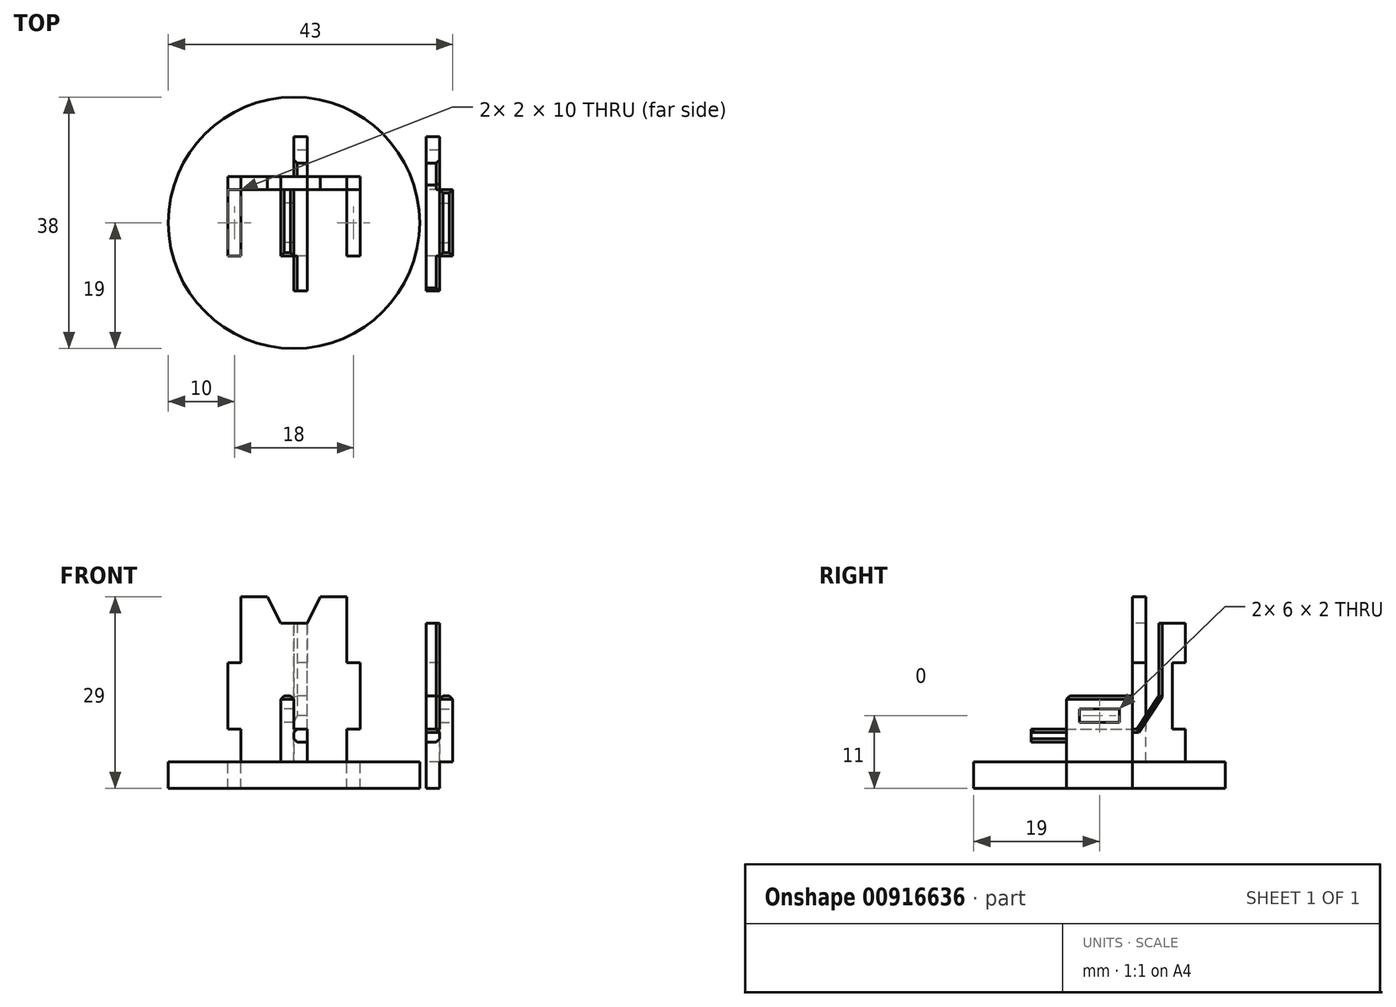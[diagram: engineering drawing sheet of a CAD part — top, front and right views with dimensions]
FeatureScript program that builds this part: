
annotation { "Feature Type Name" : "Feature", "Feature Type Description" : "" }
export const myFeature = defineFeature(function(context is Context, id is Id, definition is map)
    precondition{}
    {
        {
            var Q0;
            Q0=qCreatedBy(makeId("Top.planeOp"),FACE);
            var sketch = newSketch(context, id + "F0", { "sketchPlane" : qUnion([Q0])});
            skCircle(sketch, "E0", {"center": v(0, 0) * mm, "radius": 19 * mm});
            skSolve(sketch);
        }
        {
            var Q0;
            Q0=makeQuery(id+"F0.imprint","IMPRINT",FACE,{"disambiguationData":[TD([[makeQuery(id+"F0.imprint","IMPRINT",EDGE,{"derivedFrom":sQuery(id+"F0.wireOp",EDGE,"E0")}),1.0]])]});
            extrude(context, id + "F1", {"entities" : qUnion([Q0]), "depth" : 4 * mm, "offsetDistance" : 25 * mm});
        }
        {
            var Q0;
            Q0=makeQuery(id+"F1.opExtrude","CAP_FACE",FACE,{"disambiguationData":[OSD([sQuery(id+"F0.wireOp",EDGE,"E0")])],"isStart":false});
            var sketch = newSketch(context, id + "F2", { "sketchPlane" : qUnion([Q0])});
            skLineSegment(sketch, "E1.bottom", {"start": v(-10, 5) * mm, "end": v(-8, 5) * mm});
            skLineSegment(sketch, "E1.top", {"start": v(-10, -5) * mm, "end": v(-8, -5) * mm});
            skLineSegment(sketch, "E1.left", {"start": v(-10, 5) * mm, "end": v(-10, -5) * mm});
            skLineSegment(sketch, "E1.right", {"start": v(-8, 5) * mm, "end": v(-8, -5) * mm});
            skLineSegment(sketch, "E2", {"start": v(0, -13.87) * mm, "end": v(0, 16.66) * mm, "construction": true});
            skLineSegment(sketch, "E3.MirrorCS", {"start": v(10, 5) * mm, "end": v(8, 5) * mm});
            skLineSegment(sketch, "E4.MirrorCS", {"start": v(10, 5) * mm, "end": v(10, -5) * mm});
            skLineSegment(sketch, "E5.MirrorCS", {"start": v(8, 5) * mm, "end": v(8, -5) * mm});
            skLineSegment(sketch, "E6.MirrorCS", {"start": v(10, -5) * mm, "end": v(8, -5) * mm});
            skSolve(sketch);
        }
        {
            var Q0;
            Q0=makeQuery(id+"F2.imprint","IMPRINT",FACE,{"disambiguationData":[TD([[makeQuery(id+"F2.imprint","IMPRINT",EDGE,{"derivedFrom":sQuery(id+"F2.wireOp",EDGE,"E1.bottom")}),-1.0]])]});
            var Q1;
            Q1=makeQuery(id+"F2.imprint","IMPRINT",FACE,{"disambiguationData":[TD([[makeQuery(id+"F2.imprint","IMPRINT",EDGE,{"derivedFrom":sQuery(id+"F2.wireOp",EDGE,"E3.MirrorCS")}),1.0]])]});
            extrude(context, id + "F3", {"entities" : qUnion([Q0, Q1]), "operationType" : NewBodyOperationType.REMOVE, "endBound" : BoundingType.THROUGH_ALL, "oppositeDirection" : true, "depth" : 4 * mm, "offsetDistance" : 25 * mm});
        }
        {
            var Q0;
            Q0=qCreatedBy(makeId("Right.planeOp"),FACE);
            var sketch = newSketch(context, id + "F4", { "sketchPlane" : qUnion([Q0])});
            skLineSegment(sketch, "E7", {"start": v(-5, 0) * mm, "end": v(-5, 4) * mm});
            skLineSegment(sketch, "E8", {"start": v(-5, 4) * mm, "end": v(-5, 7) * mm});
            skLineSegment(sketch, "E9", {"start": v(-5, 7) * mm, "end": v(-10.32, 7) * mm});
            skLineSegment(sketch, "E10", {"start": v(-10.32, 7) * mm, "end": v(-10.32, 9) * mm});
            skLineSegment(sketch, "E11", {"start": v(-10.32, 9) * mm, "end": v(5.68, 9) * mm});
            skLineSegment(sketch, "E12", {"start": v(5.68, 9) * mm, "end": v(9, 14) * mm});
            skLineSegment(sketch, "E13", {"start": v(9, 14) * mm, "end": v(9, 29) * mm});
            skLineSegment(sketch, "E14", {"start": v(9, 29) * mm, "end": v(13, 29) * mm});
            skLineSegment(sketch, "E15", {"start": v(13, 29) * mm, "end": v(13, 4) * mm});
            skLineSegment(sketch, "E16", {"start": v(13, 4) * mm, "end": v(5, 4) * mm});
            skLineSegment(sketch, "E17", {"start": v(5, 4) * mm, "end": v(5, 0) * mm});
            skLineSegment(sketch, "E18", {"start": v(5, 0) * mm, "end": v(-5, 0) * mm});
            skSolve(sketch);
        }
        {
            var Q0;
            Q0=makeQuery(id+"F4.imprint","IMPRINT",FACE,{"disambiguationData":[TD([[makeQuery(id+"F4.imprint","IMPRINT",EDGE,{"derivedFrom":sQuery(id+"F4.wireOp",EDGE,"E7")}),-1.0]])]});
            extrude(context, id + "F5", {"entities" : qUnion([Q0]), "depth" : 2 * mm, "offsetDistance" : 25 * mm});
        }
        {
            var Q0;
            Q0=makeQuery(id+"F5.opExtrude","CAP_FACE",FACE,{"disambiguationData":[OSD([sQuery(id+"F4.wireOp",EDGE,"E7"),sQuery(id+"F4.wireOp",EDGE,"E8"),sQuery(id+"F4.wireOp",EDGE,"E9"),sQuery(id+"F4.wireOp",EDGE,"E10"),sQuery(id+"F4.wireOp",EDGE,"E11"),sQuery(id+"F4.wireOp",EDGE,"E12"),sQuery(id+"F4.wireOp",EDGE,"E13"),sQuery(id+"F4.wireOp",EDGE,"E14"),sQuery(id+"F4.wireOp",EDGE,"E15"),sQuery(id+"F4.wireOp",EDGE,"E16"),sQuery(id+"F4.wireOp",EDGE,"E17"),sQuery(id+"F4.wireOp",EDGE,"E18")])],"isStart":true});
            var sketch = newSketch(context, id + "F6", { "sketchPlane" : qUnion([Q0])});
            skLineSegment(sketch, "E19.bottom", {"start": v(-13, 19) * mm, "end": v(-11, 19) * mm});
            skLineSegment(sketch, "E19.top", {"start": v(-13, 9) * mm, "end": v(-11, 9) * mm});
            skLineSegment(sketch, "E19.left", {"start": v(-13, 19) * mm, "end": v(-13, 9) * mm});
            skLineSegment(sketch, "E19.right", {"start": v(-11, 19) * mm, "end": v(-11, 9) * mm});
            skSolve(sketch);
        }
        {
            var Q0;
            Q0=makeQuery(id+"F1.opExtrude","CAP_FACE",FACE,{"disambiguationData":[OSD([sQuery(id+"F0.wireOp",EDGE,"E0")])],"isStart":false});
            var sketch = newSketch(context, id + "F7", { "sketchPlane" : qUnion([Q0])});
            skLineSegment(sketch, "E20.bottom", {"start": v(-10, 5) * mm, "end": v(10, 5) * mm});
            skLineSegment(sketch, "E20.top", {"start": v(-10, 7) * mm, "end": v(10, 7) * mm});
            skLineSegment(sketch, "E20.left", {"start": v(-10, 5) * mm, "end": v(-10, 7) * mm});
            skLineSegment(sketch, "E20.right", {"start": v(10, 5) * mm, "end": v(10, 7) * mm});
            skSolve(sketch);
        }
        {
            var Q0;
            Q0=makeQuery(id+"F7.imprint","IMPRINT",FACE,{"disambiguationData":[TD([[makeQuery(id+"F7.imprint","IMPRINT",EDGE,{"derivedFrom":sQuery(id+"F7.wireOp",EDGE,"E20.top")}),-1.0]])]});
            extrude(context, id + "F8", {"entities" : qUnion([Q0]), "depth" : 25 * mm, "offsetDistance" : 25 * mm});
        }
        {
            var Q0;
            Q0=makeQuery(id+"F8.opExtrude","SWEPT_FACE",FACE,{"disambiguationData":[OSD([sQuery(id+"F7.wireOp",EDGE,"E20.top")])]});
            var sketch = newSketch(context, id + "F9", { "sketchPlane" : qUnion([Q0])});
            skLineSegment(sketch, "E21.bottom", {"start": v(-10, 29) * mm, "end": v(-8, 29) * mm});
            skLineSegment(sketch, "E21.top", {"start": v(-10, 19) * mm, "end": v(-8, 19) * mm});
            skLineSegment(sketch, "E21.left", {"start": v(-10, 29) * mm, "end": v(-10, 19) * mm});
            skLineSegment(sketch, "E21.right", {"start": v(-8, 29) * mm, "end": v(-8, 19) * mm});
            skLineSegment(sketch, "E22.bottom", {"start": v(10, 29) * mm, "end": v(8, 29) * mm});
            skLineSegment(sketch, "E22.top", {"start": v(10, 19) * mm, "end": v(8, 19) * mm});
            skLineSegment(sketch, "E22.left", {"start": v(10, 29) * mm, "end": v(10, 19) * mm});
            skLineSegment(sketch, "E22.right", {"start": v(8, 29) * mm, "end": v(8, 19) * mm});
            skLineSegment(sketch, "E23.bottom", {"start": v(-10, 4) * mm, "end": v(-8, 4) * mm});
            skLineSegment(sketch, "E23.top", {"start": v(-10, 9) * mm, "end": v(-8, 9) * mm});
            skLineSegment(sketch, "E23.left", {"start": v(-10, 4) * mm, "end": v(-10, 9) * mm});
            skLineSegment(sketch, "E23.right", {"start": v(-8, 4) * mm, "end": v(-8, 9) * mm});
            skLineSegment(sketch, "E24.bottom", {"start": v(10, 4) * mm, "end": v(8, 4) * mm});
            skLineSegment(sketch, "E24.top", {"start": v(10, 9) * mm, "end": v(8, 9) * mm});
            skLineSegment(sketch, "E24.left", {"start": v(10, 4) * mm, "end": v(10, 9) * mm});
            skLineSegment(sketch, "E24.right", {"start": v(8, 4) * mm, "end": v(8, 9) * mm});
            skSolve(sketch);
        }
        {
            var Q0;
            Q0=makeQuery(id+"F9.imprint","IMPRINT",FACE,{"disambiguationData":[TD([[makeQuery(id+"F9.imprint","IMPRINT",EDGE,{"derivedFrom":sQuery(id+"F9.wireOp",EDGE,"E21.bottom")}),1.0]])]});
            var Q1;
            Q1=makeQuery(id+"F9.imprint","IMPRINT",FACE,{"disambiguationData":[TD([[makeQuery(id+"F9.imprint","IMPRINT",EDGE,{"derivedFrom":sQuery(id+"F9.wireOp",EDGE,"E22.bottom")}),1.0]])]});
            var Q2;
            Q2=makeQuery(id+"F9.imprint","IMPRINT",FACE,{"disambiguationData":[TD([[makeQuery(id+"F9.imprint","IMPRINT",EDGE,{"derivedFrom":sQuery(id+"F9.wireOp",EDGE,"E24.bottom")}),-1.0]])]});
            var Q3;
            Q3=makeQuery(id+"F9.imprint","IMPRINT",FACE,{"disambiguationData":[TD([[makeQuery(id+"F9.imprint","IMPRINT",EDGE,{"derivedFrom":sQuery(id+"F9.wireOp",EDGE,"E23.bottom")}),-1.0]])]});
            extrude(context, id + "F10", {"entities" : qUnion([Q0, Q1, Q2, Q3]), "operationType" : NewBodyOperationType.REMOVE, "endBound" : BoundingType.THROUGH_ALL, "oppositeDirection" : true, "depth" : 25 * mm, "offsetDistance" : 25 * mm});
        }
        {
            var Q0;
            Q0=makeQuery(id+"F6.imprint","IMPRINT",FACE,{"disambiguationData":[TD([[makeQuery(id+"F6.imprint","IMPRINT",EDGE,{"derivedFrom":sQuery(id+"F6.wireOp",EDGE,"E19.bottom")}),-1.0]])]});
            extrude(context, id + "F11", {"entities" : qUnion([Q0]), "operationType" : NewBodyOperationType.REMOVE, "endBound" : BoundingType.THROUGH_ALL, "oppositeDirection" : true, "depth" : 25 * mm, "offsetDistance" : 25 * mm});
        }
        {
            var Q0;
            Q0=makeQuery(id+"F8.opExtrude","SWEPT_FACE",FACE,{"disambiguationData":[OSD([sQuery(id+"F7.wireOp",EDGE,"E20.bottom")])]});
            var sketch = newSketch(context, id + "F12", { "sketchPlane" : qUnion([Q0])});
            skLineSegment(sketch, "E25", {"start": v(-4, 29) * mm, "end": v(-2, 25) * mm});
            skLineSegment(sketch, "E26", {"start": v(-2, 25) * mm, "end": v(2, 25) * mm});
            skLineSegment(sketch, "E27", {"start": v(2, 25) * mm, "end": v(4, 29) * mm});
            skLineSegment(sketch, "E28", {"start": v(4, 29) * mm, "end": v(-4, 29) * mm});
            skSolve(sketch);
        }
        {
            var Q0;
            Q0=makeQuery(id+"F12.imprint","IMPRINT",FACE,{"disambiguationData":[TD([[makeQuery(id+"F12.imprint","IMPRINT",EDGE,{"derivedFrom":sQuery(id+"F12.wireOp",EDGE,"E25")}),1.0]])]});
            extrude(context, id + "F13", {"entities" : qUnion([Q0]), "operationType" : NewBodyOperationType.REMOVE, "endBound" : BoundingType.THROUGH_ALL, "oppositeDirection" : true, "depth" : 25 * mm, "offsetDistance" : 25 * mm});
        }
        {
            var Q0;
            Q0=makeQuery(id+"F5.opExtrude","SWEPT_BODY",BODY,{"disambiguationData":[OSD([sQuery(id+"F4.wireOp",EDGE,"E7"),sQuery(id+"F4.wireOp",EDGE,"E8"),sQuery(id+"F4.wireOp",EDGE,"E9"),sQuery(id+"F4.wireOp",EDGE,"E10"),sQuery(id+"F4.wireOp",EDGE,"E11"),sQuery(id+"F4.wireOp",EDGE,"E12"),sQuery(id+"F4.wireOp",EDGE,"E13"),sQuery(id+"F4.wireOp",EDGE,"E14"),sQuery(id+"F4.wireOp",EDGE,"E15"),sQuery(id+"F4.wireOp",EDGE,"E16"),sQuery(id+"F4.wireOp",EDGE,"E17"),sQuery(id+"F4.wireOp",EDGE,"E18")])]});
            transform(context, id + "F14", {"entities" : qUnion([Q0]), "transformType" : TransformType.TRANSLATION_3D, "dx" : 20 * mm, "dy" : 0 * mm, "dz" : 0 * mm, "makeCopy" : true});
        }
        {
            var Q0;
            Q0=makeQuery(id+"F5.opExtrude","CAP_FACE",FACE,{"disambiguationData":[OSD([sQuery(id+"F4.wireOp",EDGE,"E7"),sQuery(id+"F4.wireOp",EDGE,"E8"),sQuery(id+"F4.wireOp",EDGE,"E9"),sQuery(id+"F4.wireOp",EDGE,"E10"),sQuery(id+"F4.wireOp",EDGE,"E11"),sQuery(id+"F4.wireOp",EDGE,"E12"),sQuery(id+"F4.wireOp",EDGE,"E13"),sQuery(id+"F4.wireOp",EDGE,"E14"),sQuery(id+"F4.wireOp",EDGE,"E15"),sQuery(id+"F4.wireOp",EDGE,"E16"),sQuery(id+"F4.wireOp",EDGE,"E17"),sQuery(id+"F4.wireOp",EDGE,"E18")])],"isStart":true});
            var sketch = newSketch(context, id + "F15", { "sketchPlane" : qUnion([Q0])});
            skLineSegment(sketch, "E29.bottom", {"start": v(-5, 4) * mm, "end": v(5, 4) * mm});
            skLineSegment(sketch, "E29.top", {"start": v(-5, 14) * mm, "end": v(5, 14) * mm});
            skLineSegment(sketch, "E29.left", {"start": v(-5, 4) * mm, "end": v(-5, 14) * mm});
            skLineSegment(sketch, "E29.right", {"start": v(5, 4) * mm, "end": v(5, 14) * mm});
            skSolve(sketch);
        }
        {
            var Q0;
            {var subQ0=sQuery(id+"F15.wireOp",EDGE,"E29.top");Q0=makeQuery(id+"F15.imprint","IMPRINT",FACE,{"disambiguationData":[TD([[makeQuery(id+"F15.imprint","IMPRINT",EDGE,{"derivedFrom":subQ0}),-1.0]])]});}
            var Q1;
            {var subQ2=sQuery(id+"F15.wireOp",EDGE,"E29.bottom");Q1=makeQuery(id+"F15.imprint","IMPRINT",FACE,{"disambiguationData":[TD([[makeQuery(id+"F15.imprint","IMPRINT",EDGE,{"derivedFrom":subQ2}),1.0]])]});}
            extrude(context, id + "F16", {"entities" : qUnion([Q0, Q1]), "operationType" : NewBodyOperationType.ADD, "depth" : 2 * mm, "offsetDistance" : 25 * mm});
        }
        {
            var Q0;
            Q0=makeQuery(id+"F16.opExtrude","CAP_FACE",FACE,{"disambiguationData":[OSD([sQuery(id+"F15.wireOp",EDGE,"E29.bottom"),sQuery(id+"F15.wireOp",EDGE,"E29.top"),sQuery(id+"F15.wireOp",EDGE,"E29.left"),sQuery(id+"F15.wireOp",EDGE,"E29.right")])],"isStart":false});
            var sketch = newSketch(context, id + "F17", { "sketchPlane" : qUnion([Q0])});
            skLineSegment(sketch, "E30.bottom", {"start": v(-3, 12) * mm, "end": v(3, 12) * mm});
            skLineSegment(sketch, "E30.top", {"start": v(-3, 10) * mm, "end": v(3, 10) * mm});
            skLineSegment(sketch, "E30.left", {"start": v(-3, 12) * mm, "end": v(-3, 10) * mm});
            skLineSegment(sketch, "E30.right", {"start": v(3, 12) * mm, "end": v(3, 10) * mm});
            skSolve(sketch);
        }
        {
            var Q0;
            Q0=makeQuery(id+"F17.imprint","IMPRINT",FACE,{"disambiguationData":[TD([[makeQuery(id+"F17.imprint","IMPRINT",EDGE,{"derivedFrom":sQuery(id+"F17.wireOp",EDGE,"E30.bottom")}),-1.0]])]});
            extrude(context, id + "F18", {"entities" : qUnion([Q0]), "operationType" : NewBodyOperationType.REMOVE, "endBound" : BoundingType.THROUGH_ALL, "oppositeDirection" : true, "depth" : 25 * mm, "offsetDistance" : 25 * mm});
        }
        {
            var Q0;
            Q0=makeQuery(id+"F14.opPattern","COPY",FACE,{"derivedFrom":makeQuery(id+"F5.opExtrude","CAP_FACE",FACE,{"disambiguationData":[OSD([sQuery(id+"F4.wireOp",EDGE,"E7"),sQuery(id+"F4.wireOp",EDGE,"E8"),sQuery(id+"F4.wireOp",EDGE,"E9"),sQuery(id+"F4.wireOp",EDGE,"E10"),sQuery(id+"F4.wireOp",EDGE,"E11"),sQuery(id+"F4.wireOp",EDGE,"E12"),sQuery(id+"F4.wireOp",EDGE,"E13"),sQuery(id+"F4.wireOp",EDGE,"E14"),sQuery(id+"F4.wireOp",EDGE,"E15"),sQuery(id+"F4.wireOp",EDGE,"E16"),sQuery(id+"F4.wireOp",EDGE,"E17"),sQuery(id+"F4.wireOp",EDGE,"E18")])],"isStart":false}),"instanceName":"1"});
            var sketch = newSketch(context, id + "F19", { "sketchPlane" : qUnion([Q0])});
            skPoint(sketch, "E31.oppositeSnap0", {"position": v(-5, 3.5) * mm});
            skLineSegment(sketch, "E31.bottom", {"start": v(5, 4) * mm, "end": v(-5, 4) * mm});
            skLineSegment(sketch, "E31.top", {"start": v(5, 14) * mm, "end": v(-5, 14) * mm});
            skLineSegment(sketch, "E31.left", {"start": v(5, 4) * mm, "end": v(5, 14) * mm});
            skLineSegment(sketch, "E31.right", {"start": v(-5, 4) * mm, "end": v(-5, 14) * mm});
            skSolve(sketch);
        }
        {
            var Q0;
            {var subQ0=sQuery(id+"F19.wireOp",EDGE,"E31.top");Q0=makeQuery(id+"F19.imprint","IMPRINT",FACE,{"disambiguationData":[TD([[makeQuery(id+"F19.imprint","IMPRINT",EDGE,{"derivedFrom":subQ0}),1.0]])]});}
            var Q1;
            {var subQ2=sQuery(id+"F19.wireOp",EDGE,"E31.bottom");Q1=makeQuery(id+"F19.imprint","IMPRINT",FACE,{"disambiguationData":[TD([[makeQuery(id+"F19.imprint","IMPRINT",EDGE,{"derivedFrom":subQ2}),-1.0]])]});}
            extrude(context, id + "F20", {"entities" : qUnion([Q0, Q1]), "operationType" : NewBodyOperationType.ADD, "depth" : 2 * mm, "offsetDistance" : 25 * mm});
        }
        {
            var Q0;
            Q0=makeQuery(id+"F20.opExtrude","CAP_FACE",FACE,{"disambiguationData":[OSD([sQuery(id+"F19.wireOp",EDGE,"E31.bottom"),sQuery(id+"F19.wireOp",EDGE,"E31.top"),sQuery(id+"F19.wireOp",EDGE,"E31.left"),sQuery(id+"F19.wireOp",EDGE,"E31.right")])],"isStart":false});
            var sketch = newSketch(context, id + "F21", { "sketchPlane" : qUnion([Q0])});
            skLineSegment(sketch, "E32.bottom", {"start": v(-3, 12) * mm, "end": v(3, 12) * mm});
            skLineSegment(sketch, "E32.top", {"start": v(-3, 10) * mm, "end": v(3, 10) * mm});
            skLineSegment(sketch, "E32.left", {"start": v(-3, 12) * mm, "end": v(-3, 10) * mm});
            skLineSegment(sketch, "E32.right", {"start": v(3, 12) * mm, "end": v(3, 10) * mm});
            skSolve(sketch);
        }
        {
            var Q0;
            Q0=makeQuery(id+"F21.imprint","IMPRINT",FACE,{"disambiguationData":[TD([[makeQuery(id+"F21.imprint","IMPRINT",EDGE,{"derivedFrom":sQuery(id+"F21.wireOp",EDGE,"E32.bottom")}),-1.0]])]});
            extrude(context, id + "F22", {"entities" : qUnion([Q0]), "operationType" : NewBodyOperationType.REMOVE, "endBound" : BoundingType.THROUGH_ALL, "oppositeDirection" : true, "depth" : 25 * mm, "offsetDistance" : 25 * mm});
        }
        {
            var Q0;
            Q0=makeQuery(id+"F20.opExtrude","CAP_EDGE",EDGE,{"disambiguationData":[OSD([sQuery(id+"F19.wireOp",EDGE,"E31.top")])],"isStart":false});
            var Q1;
            Q1=makeQuery(id+"F20.opExtrude","SWEPT_EDGE",EDGE,{"disambiguationData":[OSD([sQuery(id+"F19.wireOp",EDGE,"E31.top"),sQuery(id+"F19.wireOp",EDGE,"E31.right")])]});
            var Q2;
            Q2=makeQuery(id+"F20.opExtrude","SWEPT_EDGE",EDGE,{"disambiguationData":[OSD([sQuery(id+"F19.wireOp",EDGE,"E31.top"),sQuery(id+"F19.wireOp",EDGE,"E31.left")])]});
            var Q3;
            Q3=makeQuery(id+"F20.opExtrude","CAP_EDGE",EDGE,{"disambiguationData":[OSD([sQuery(id+"F19.wireOp",EDGE,"E31.top")])],"isStart":true});
            var Q4;
            {var subQ0=sQuery(id+"F4.wireOp",EDGE,"E11");var subQ1=sQuery(id+"F4.wireOp",EDGE,"E10");var subQ2=sQuery(id+"F4.wireOp",EDGE,"E8");var subQ3=sQuery(id+"F4.wireOp",EDGE,"E7");var subQ4=makeQuery(id+"F14.opPattern","COPY",FACE,{"derivedFrom":makeQuery(id+"F5.opExtrude","CAP_FACE",FACE,{"disambiguationData":[OSD([subQ3,subQ2,sQuery(id+"F4.wireOp",EDGE,"E9"),subQ1,subQ0,sQuery(id+"F4.wireOp",EDGE,"E12"),sQuery(id+"F4.wireOp",EDGE,"E13"),sQuery(id+"F4.wireOp",EDGE,"E14"),sQuery(id+"F4.wireOp",EDGE,"E15"),sQuery(id+"F4.wireOp",EDGE,"E16"),sQuery(id+"F4.wireOp",EDGE,"E17"),sQuery(id+"F4.wireOp",EDGE,"E18")])],"isStart":false}),"instanceName":"1"});var subQ5=makeQuery(id+"F14.opPattern","COPY",FACE,{"derivedFrom":makeQuery(id+"F5.opExtrude","SWEPT_FACE",FACE,{"disambiguationData":[OSD([subQ0])]}),"instanceName":"1"});Q4=makeQuery(id+"F20.boolean.opBoolean","SPLIT",EDGE,{"disambiguationData":[topologyDisambiguationEdgeConnected([subQ5,subQ4]),TD([makeQuery(id+"F14.opPattern","COPY",FACE,{"derivedFrom":makeQuery(id+"F5.opExtrude","SWEPT_FACE",FACE,{"disambiguationData":[OSD([subQ1])]}),"instanceName":"1"})])],"derivedFrom":makeQuery(id+"F14.opPattern","COPY",EDGE,{"derivedFrom":makeQuery(id+"F5.opExtrude","CAP_EDGE",EDGE,{"disambiguationData":[OSD([subQ0])],"isStart":false}),"instanceName":"1"})});}
            var Q5;
            Q5=makeQuery(id+"F14.opPattern","COPY",EDGE,{"derivedFrom":makeQuery(id+"F5.opExtrude","SWEPT_EDGE",EDGE,{"disambiguationData":[OSD([sQuery(id+"F4.wireOp",EDGE,"E10"),sQuery(id+"F4.wireOp",EDGE,"E11")])]}),"instanceName":"1"});
            var Q6;
            Q6=makeQuery(id+"F14.opPattern","COPY",EDGE,{"derivedFrom":makeQuery(id+"F5.opExtrude","CAP_EDGE",EDGE,{"disambiguationData":[OSD([sQuery(id+"F4.wireOp",EDGE,"E12")])],"isStart":false}),"instanceName":"1"});
            var Q7;
            Q7=makeQuery(id+"F14.opPattern","COPY",EDGE,{"derivedFrom":makeQuery(id+"F5.opExtrude","CAP_EDGE",EDGE,{"disambiguationData":[OSD([sQuery(id+"F4.wireOp",EDGE,"E13")])],"isStart":false}),"instanceName":"1"});
            var Q8;
            Q8=makeQuery(id+"F14.opPattern","COPY",EDGE,{"derivedFrom":makeQuery(id+"F5.opExtrude","CAP_EDGE",EDGE,{"disambiguationData":[OSD([sQuery(id+"F4.wireOp",EDGE,"E14")])],"isStart":false}),"instanceName":"1"});
            var Q9;
            Q9=makeQuery(id+"F14.opPattern","COPY",EDGE,{"derivedFrom":makeQuery(id+"F5.opExtrude","CAP_EDGE",EDGE,{"disambiguationData":[OSD([sQuery(id+"F4.wireOp",EDGE,"E9")])],"isStart":false}),"instanceName":"1"});
            var Q10;
            {var subQ0=sQuery(id+"F4.wireOp",EDGE,"E10");var subQ2=sQuery(id+"F4.wireOp",EDGE,"E11");var subQ3=sQuery(id+"F4.wireOp",EDGE,"E8");var subQ4=sQuery(id+"F4.wireOp",EDGE,"E7");var subQ5=makeQuery(id+"F5.opExtrude","CAP_FACE",FACE,{"disambiguationData":[OSD([subQ4,subQ3,sQuery(id+"F4.wireOp",EDGE,"E9"),subQ0,subQ2,sQuery(id+"F4.wireOp",EDGE,"E12"),sQuery(id+"F4.wireOp",EDGE,"E13"),sQuery(id+"F4.wireOp",EDGE,"E14"),sQuery(id+"F4.wireOp",EDGE,"E15"),sQuery(id+"F4.wireOp",EDGE,"E16"),sQuery(id+"F4.wireOp",EDGE,"E17"),sQuery(id+"F4.wireOp",EDGE,"E18")])],"isStart":true});var subQ6=makeQuery(id+"F5.opExtrude","SWEPT_FACE",FACE,{"disambiguationData":[OSD([subQ2])]});Q10=makeQuery(id+"F16.boolean.opBoolean","SPLIT",EDGE,{"disambiguationData":[topologyDisambiguationEdgeConnected([subQ5,subQ6]),TD([makeQuery(id+"F5.opExtrude","SWEPT_FACE",FACE,{"disambiguationData":[OSD([subQ0])]})])],"derivedFrom":makeQuery(id+"F5.opExtrude","CAP_EDGE",EDGE,{"disambiguationData":[OSD([subQ2])],"isStart":true})});}
            var Q11;
            Q11=makeQuery(id+"F16.opExtrude","CAP_EDGE",EDGE,{"disambiguationData":[OSD([sQuery(id+"F15.wireOp",EDGE,"E29.top")])],"isStart":true});
            var Q12;
            Q12=makeQuery(id+"F16.opExtrude","SWEPT_EDGE",EDGE,{"disambiguationData":[OSD([sQuery(id+"F15.wireOp",EDGE,"E29.top"),sQuery(id+"F15.wireOp",EDGE,"E29.right")])]});
            var Q13;
            Q13=makeQuery(id+"F16.opExtrude","CAP_EDGE",EDGE,{"disambiguationData":[OSD([sQuery(id+"F15.wireOp",EDGE,"E29.top")])],"isStart":false});
            var Q14;
            Q14=makeQuery(id+"F16.opExtrude","SWEPT_EDGE",EDGE,{"disambiguationData":[OSD([sQuery(id+"F15.wireOp",EDGE,"E29.top"),sQuery(id+"F15.wireOp",EDGE,"E29.left")])]});
            var Q15;
            Q15=makeQuery(id+"F5.opExtrude","CAP_EDGE",EDGE,{"disambiguationData":[OSD([sQuery(id+"F4.wireOp",EDGE,"E12")])],"isStart":true});
            var Q16;
            Q16=makeQuery(id+"F5.opExtrude","CAP_EDGE",EDGE,{"disambiguationData":[OSD([sQuery(id+"F4.wireOp",EDGE,"E13")])],"isStart":true});
            var Q17;
            Q17=makeQuery(id+"F5.opExtrude","CAP_EDGE",EDGE,{"disambiguationData":[OSD([sQuery(id+"F4.wireOp",EDGE,"E14")])],"isStart":true});
            var Q18;
            Q18=makeQuery(id+"F5.opExtrude","CAP_EDGE",EDGE,{"disambiguationData":[OSD([sQuery(id+"F4.wireOp",EDGE,"E9")])],"isStart":true});
            chamfer(context, id + "F23", {"entities" : qUnion([Q0, Q1, Q2, Q3, Q4, Q5, Q6, Q7, Q8, Q9, Q10, Q11, Q12, Q13, Q14, Q15, Q16, Q17, Q18]), "width" : 0.5 * mm, "tangentPropagation" : true});
        }
    });
